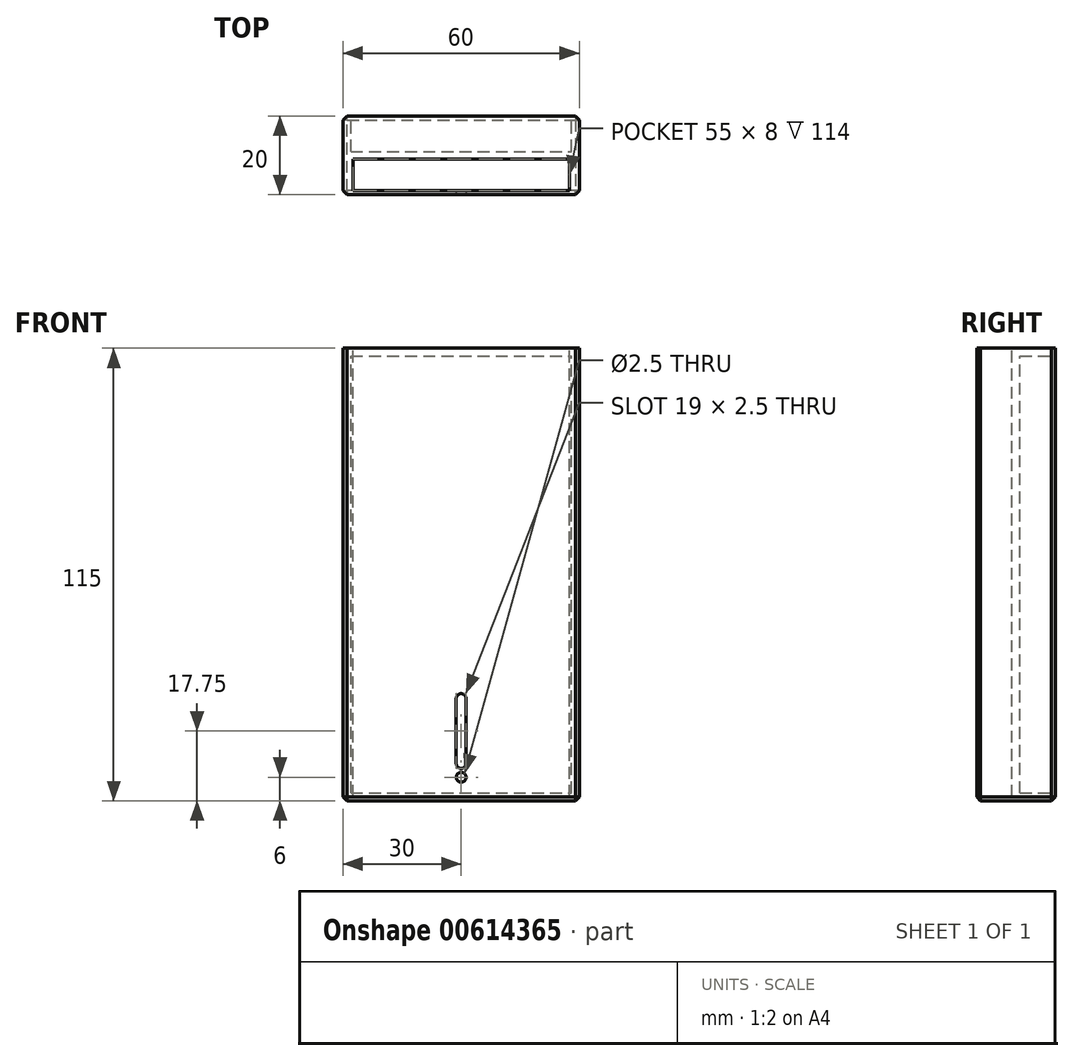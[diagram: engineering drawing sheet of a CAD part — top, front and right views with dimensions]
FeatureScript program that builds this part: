
annotation { "Feature Type Name" : "Feature", "Feature Type Description" : "" }
export const myFeature = defineFeature(function(context is Context, id is Id, definition is map)
    precondition{}
    {
        {
            var Q0;
            Q0=qCreatedBy(makeId("Front.planeOp"),FACE);
            var sketch = newSketch(context, id + "F0", { "sketchPlane" : qUnion([Q0])});
            skLineSegment(sketch, "E0.bottom", {"start": v(0, 0) * mm, "end": v(60, 0) * mm});
            skLineSegment(sketch, "E0.top", {"start": v(0, 115) * mm, "end": v(60, 115) * mm});
            skLineSegment(sketch, "E0.left", {"start": v(0, 0) * mm, "end": v(0, 115) * mm});
            skLineSegment(sketch, "E0.right", {"start": v(60, 0) * mm, "end": v(60, 115) * mm});
            skSolve(sketch);
        }
        {
            var Q0;
            Q0=makeQuery(id+"F0.imprint","IMPRINT",FACE,{"disambiguationData":[TD([[makeQuery(id+"F0.imprint","IMPRINT",EDGE,{"derivedFrom":sQuery(id+"F0.wireOp",EDGE,"E0.bottom")}),1.0]])]});
            extrude(context, id + "F1", {"entities" : qUnion([Q0]), "depth" : 20 * mm, "offsetDistance" : 25 * mm});
        }
        {
            var Q0;
            Q0=makeQuery(id+"F1.opExtrude","SWEPT_FACE",FACE,{"disambiguationData":[OSD([sQuery(id+"F0.wireOp",EDGE,"E0.top")])]});
            var sketch = newSketch(context, id + "F2", { "sketchPlane" : qUnion([Q0])});
            skLineSegment(sketch, "E1", {"start": v(2.5, -10) * mm, "end": v(57.5, -10) * mm, "construction": true});
            skPoint(sketch, "E2.orphan", {"position": v(60, -10) * mm});
            skPoint(sketch, "E3.orphan", {"position": v(0, -10) * mm});
            skLineSegment(sketch, "E4.0", {"start": v(2.5, -19) * mm, "end": v(57.5, -19) * mm});
            skLineSegment(sketch, "E5.0", {"start": v(2.5, -11) * mm, "end": v(57.5, -11) * mm});
            skLineSegment(sketch, "E6", {"start": v(2.5, -11) * mm, "end": v(2.5, -19) * mm});
            skLineSegment(sketch, "E7", {"start": v(57.5, -11) * mm, "end": v(57.5, -19) * mm});
            skSolve(sketch);
        }
        {
            var Q0;
            Q0=makeQuery(id+"F1.opExtrude","CAP_FACE",FACE,{"disambiguationData":[OSD([sQuery(id+"F0.wireOp",EDGE,"E0.bottom"),sQuery(id+"F0.wireOp",EDGE,"E0.top"),sQuery(id+"F0.wireOp",EDGE,"E0.left"),sQuery(id+"F0.wireOp",EDGE,"E0.right")])],"isStart":true});
            var sketch = newSketch(context, id + "F3", { "sketchPlane" : qUnion([Q0])});
            skLineSegment(sketch, "E8.0", {"start": v(-2, 113) * mm, "end": v(-58, 113) * mm});
            skLineSegment(sketch, "E8.1", {"start": v(-2, 2) * mm, "end": v(-2, 113) * mm});
            skLineSegment(sketch, "E8.2", {"start": v(-2, 2) * mm, "end": v(-58, 2) * mm});
            skLineSegment(sketch, "E8.3", {"start": v(-58, 2) * mm, "end": v(-58, 113) * mm});
            skSolve(sketch);
        }
        {
            var Q0;
            Q0=makeQuery(id+"F3.imprint","IMPRINT",FACE,{"disambiguationData":[TD([[makeQuery(id+"F3.imprint","IMPRINT",EDGE,{"derivedFrom":sQuery(id+"F3.wireOp",EDGE,"E8.0")}),1.0]])]});
            extrude(context, id + "F4", {"entities" : qUnion([Q0]), "operationType" : NewBodyOperationType.REMOVE, "oppositeDirection" : true, "depth" : 9 * mm, "offsetDistance" : 25 * mm});
        }
        {
            var Q0;
            Q0=makeQuery(id+"F2.imprint","IMPRINT",FACE,{"disambiguationData":[TD([[makeQuery(id+"F2.imprint","IMPRINT",EDGE,{"derivedFrom":sQuery(id+"F2.wireOp",EDGE,"E4.0")}),1.0]])]});
            extrude(context, id + "F5", {"entities" : qUnion([Q0]), "operationType" : NewBodyOperationType.REMOVE, "oppositeDirection" : true, "depth" : 114 * mm, "offsetDistance" : 25 * mm});
        }
        {
            var Q0;
            Q0=makeQuery(id+"F1.opExtrude","CAP_FACE",FACE,{"disambiguationData":[OSD([sQuery(id+"F0.wireOp",EDGE,"E0.bottom"),sQuery(id+"F0.wireOp",EDGE,"E0.top"),sQuery(id+"F0.wireOp",EDGE,"E0.left"),sQuery(id+"F0.wireOp",EDGE,"E0.right")])],"isStart":false});
            var sketch = newSketch(context, id + "F6", { "sketchPlane" : qUnion([Q0])});
            skPoint(sketch, "E9", {"position": v(30, 6) * mm});
            skPoint(sketch, "E9.positionSnap0", {"position": v(30, 0) * mm});
            skCircle(sketch, "E10", {"center": v(30, 6) * mm, "radius": 1.25 * mm});
            skLineSegment(sketch, "E11", {"start": v(28.75, 9.5) * mm, "end": v(28.75, 26) * mm});
            skLineSegment(sketch, "E12", {"start": v(30, 115) * mm, "end": v(30, 0) * mm, "construction": true});
            skLineSegment(sketch, "E13.MirrorCS", {"start": v(31.25, 9.5) * mm, "end": v(31.25, 26) * mm});
            skLineSegment(sketch, "E14", {"start": v(28.75, 26) * mm, "end": v(31.25, 26) * mm, "construction": true});
            skArc(sketch, "E15", {"start": v(31.25, 26) * mm, "mid": v(30, 27.25) * mm, "end": v(28.75, 26) * mm});
            skArc(sketch, "E16", {"start": v(28.75, 9.5) * mm, "mid": v(30, 8.25) * mm, "end": v(31.25, 9.5) * mm});
            skPoint(sketch, "E17.orphan", {"position": v(28.75, 6) * mm});
            skPoint(sketch, "E18.orphan", {"position": v(31.25, 6) * mm});
            skSolve(sketch);
        }
        {
            var Q0;
            Q0=makeQuery(id+"F6.imprint","IMPRINT",FACE,{"disambiguationData":[TD([[makeQuery(id+"F6.imprint","IMPRINT",EDGE,{"derivedFrom":sQuery(id+"F6.wireOp",EDGE,"E11")}),-1.0]])]});
            var Q1;
            Q1=makeQuery(id+"F6.imprint","IMPRINT",FACE,{"disambiguationData":[TD([[makeQuery(id+"F6.imprint","IMPRINT",EDGE,{"derivedFrom":sQuery(id+"F6.wireOp",EDGE,"E10")}),1.0]])]});
            extrude(context, id + "F7", {"entities" : qUnion([Q0, Q1]), "operationType" : NewBodyOperationType.REMOVE, "oppositeDirection" : true, "depth" : 1 * mm, "offsetDistance" : 25 * mm});
        }
        {
            var Q0;
            Q0=makeQuery(id+"F1.opExtrude","CAP_EDGE",EDGE,{"disambiguationData":[OSD([sQuery(id+"F0.wireOp",EDGE,"E0.left")])],"isStart":false});
            var Q1;
            Q1=makeQuery(id+"F1.opExtrude","CAP_EDGE",EDGE,{"disambiguationData":[OSD([sQuery(id+"F0.wireOp",EDGE,"E0.right")])],"isStart":false});
            var Q2;
            Q2=makeQuery(id+"F1.opExtrude","CAP_EDGE",EDGE,{"disambiguationData":[OSD([sQuery(id+"F0.wireOp",EDGE,"E0.bottom")])],"isStart":false});
            var Q3;
            Q3=makeQuery(id+"F1.opExtrude","SWEPT_EDGE",EDGE,{"disambiguationData":[OSD([sQuery(id+"F0.wireOp",EDGE,"E0.bottom"),sQuery(id+"F0.wireOp",EDGE,"E0.right")])]});
            var Q4;
            Q4=makeQuery(id+"F1.opExtrude","CAP_EDGE",EDGE,{"disambiguationData":[OSD([sQuery(id+"F0.wireOp",EDGE,"E0.bottom")])],"isStart":true});
            var Q5;
            Q5=makeQuery(id+"F1.opExtrude","SWEPT_EDGE",EDGE,{"disambiguationData":[OSD([sQuery(id+"F0.wireOp",EDGE,"E0.bottom"),sQuery(id+"F0.wireOp",EDGE,"E0.left")])]});
            var Q6;
            Q6=makeQuery(id+"F1.opExtrude","CAP_EDGE",EDGE,{"disambiguationData":[OSD([sQuery(id+"F0.wireOp",EDGE,"E0.left")])],"isStart":true});
            var Q7;
            Q7=makeQuery(id+"F1.opExtrude","CAP_EDGE",EDGE,{"disambiguationData":[OSD([sQuery(id+"F0.wireOp",EDGE,"E0.right")])],"isStart":true});
            chamfer(context, id + "F8", {"entities" : qUnion([Q0, Q1, Q2, Q3, Q4, Q5, Q6, Q7]), "width" : 1 * mm, "tangentPropagation" : true});
        }
    });
